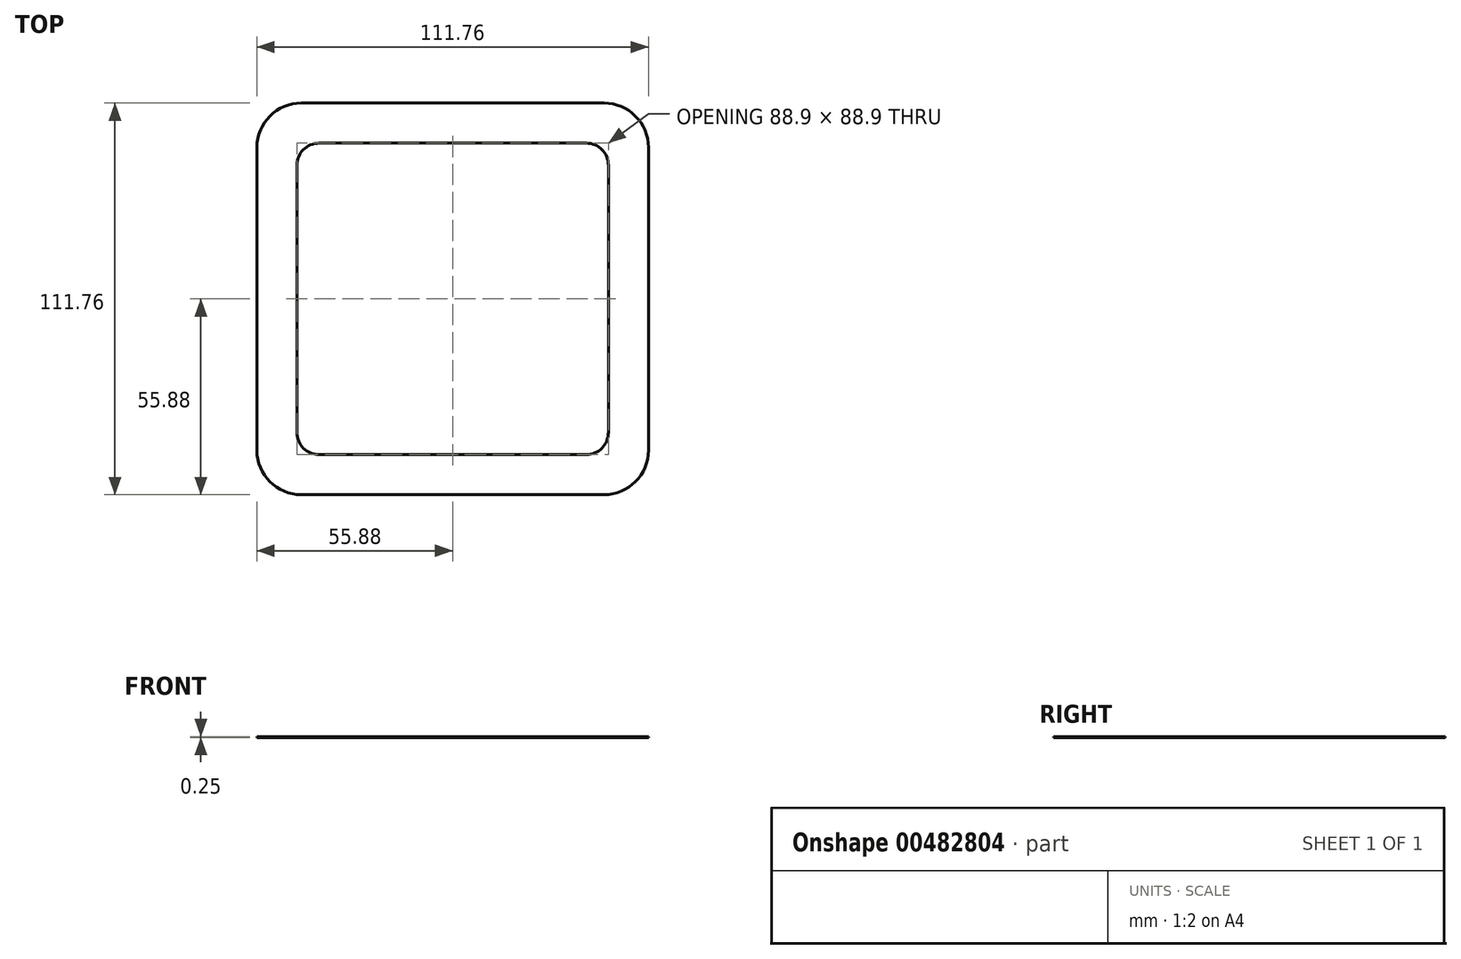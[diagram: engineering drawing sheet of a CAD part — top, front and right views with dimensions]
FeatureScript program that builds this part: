
annotation { "Feature Type Name" : "Feature", "Feature Type Description" : "" }
export const myFeature = defineFeature(function(context is Context, id is Id, definition is map)
    precondition{}
    {
        {
            var Q0;
            Q0=qCreatedBy(makeId("Top.planeOp"),FACE);
            var sketch = newSketch(context, id + "F0", { "sketchPlane" : qUnion([Q0])});
            skLineSegment(sketch, "E0.bottom", {"start": v(38.1, -44.45) * mm, "end": v(-38.1, -44.45) * mm});
            skLineSegment(sketch, "E0.top", {"start": v(38.1, 44.45) * mm, "end": v(-38.1, 44.45) * mm});
            skLineSegment(sketch, "E0.left", {"start": v(44.45, -38.1) * mm, "end": v(44.45, 38.1) * mm});
            skLineSegment(sketch, "E0.right", {"start": v(-44.45, -38.1) * mm, "end": v(-44.45, 38.1) * mm});
            skPoint(sketch, "E0.middle", {"position": v(0, 0) * mm});
            skPoint(sketch, "E1.visualSharp", {"position": v(-44.45, -44.45) * mm});
            skArc(sketch, "E1.filletArc", {"start": v(-44.45, -38.1) * mm, "mid": v(-42.6, -42.6) * mm, "end": v(-38.1, -44.45) * mm});
            skPoint(sketch, "E2.visualSharp", {"position": v(-44.45, 44.45) * mm});
            skArc(sketch, "E2.filletArc", {"start": v(-38.1, 44.45) * mm, "mid": v(-42.6, 42.6) * mm, "end": v(-44.45, 38.1) * mm});
            skPoint(sketch, "E3.visualSharp", {"position": v(44.45, 44.45) * mm});
            skArc(sketch, "E3.filletArc", {"start": v(44.45, 38.1) * mm, "mid": v(42.6, 42.6) * mm, "end": v(38.1, 44.45) * mm});
            skPoint(sketch, "E4.visualSharp", {"position": v(44.45, -44.45) * mm});
            skArc(sketch, "E4.filletArc", {"start": v(38.1, -44.45) * mm, "mid": v(42.6, -42.6) * mm, "end": v(44.45, -38.1) * mm});
            skLineSegment(sketch, "E5.bottom", {"start": v(43.18, -55.88) * mm, "end": v(-43.18, -55.88) * mm});
            skLineSegment(sketch, "E5.top", {"start": v(43.18, 55.88) * mm, "end": v(-43.18, 55.88) * mm});
            skLineSegment(sketch, "E5.left", {"start": v(55.88, -43.18) * mm, "end": v(55.88, 43.18) * mm});
            skLineSegment(sketch, "E5.right", {"start": v(-55.88, -43.18) * mm, "end": v(-55.88, 43.18) * mm});
            skPoint(sketch, "E6.visualSharp", {"position": v(-55.88, 55.88) * mm});
            skArc(sketch, "E6.filletArc", {"start": v(-43.18, 55.88) * mm, "mid": v(-52.16, 52.16) * mm, "end": v(-55.88, 43.18) * mm});
            skPoint(sketch, "E7.visualSharp", {"position": v(-55.88, -55.88) * mm});
            skArc(sketch, "E7.filletArc", {"start": v(-55.88, -43.18) * mm, "mid": v(-52.16, -52.16) * mm, "end": v(-43.18, -55.88) * mm});
            skPoint(sketch, "E8.visualSharp", {"position": v(55.88, -55.88) * mm});
            skArc(sketch, "E8.filletArc", {"start": v(43.18, -55.88) * mm, "mid": v(52.16, -52.16) * mm, "end": v(55.88, -43.18) * mm});
            skPoint(sketch, "E9.visualSharp", {"position": v(55.88, 55.88) * mm});
            skArc(sketch, "E9.filletArc", {"start": v(55.88, 43.18) * mm, "mid": v(52.16, 52.16) * mm, "end": v(43.18, 55.88) * mm});
            skSolve(sketch);
        }
        {
            var Q0;
            Q0=qSketchRegion(id+"F0",true);
            extrude(context, id + "F1", {"entities" : qUnion([Q0]), "depth" : 0.25 * mm});
        }
    });
